# Revit family: Sink_Floor_8_Inch_Round-Zurn-FS8-5-Inch-Sump
name_source: partatom
category: Plumbing Fixtures
units: mm (PartAtom-declared; Revit-internal decimal feet)

## family parameters
Always vertical = Yes
Cut with Voids When Loaded = No
Maintain Annotation Orientation = No
OmniClass Number = 23.70.50.21.24.14
OmniClass Title = Deck Waste Water Drains
Part Type = Normal
Room Calculation Point = No
Round Connector Dimension = Use Radius
Shared = No
Work Plane-Based = No

## types (3) — shared parameters
Assembly Code = D2030300
Body Range = 5 "
CW Connection = No
Default Elevation = 20 "
Description = 8 [203] DIAMETER SANITARY PVC FLOOR SINK WITH 5 [127] SUMP DEPTH
Frame Height = 1.5 "
HW Connection = No
Main Material = Polyvinyl Chloride - Zurn - Polished
Manufacturer = Zurn Water, LLC
Manufacurer Brand = Zurn
Model = FS8
Modified Date = 12/12/2025
Overall Height = 7 "
Product Documentation Link = https://files.zurn.com
Product Installation Sheet = https://files.zurn.com
Product Page URL = https://www.zurn.com
Product data url = https://www.bimobject.com
Sanitary PVC floor sink = 10.625 "
URL = www.zurn.com
Vent Connection = No
WFU = 1
Waste Connection = Yes
Width = 8.625 "
zero-valued in all types: CWFU, HWFU

## per-type parameters (varying)
| type | Pipe Size A (Actual Radius) | Pipe Size A (Inner Radius) | Pipe Size A (Nominal Radius) |
| FS8-5-PV2-2 Inch Outlet | 1.188 " | 1.034 " | 1 " |
| FS8-5-PV3-3 Inch Outlet | 1.75 " | 1.534 " | 1.5 " |
| FS8-5-PV4-4 Inch Outlet | 2.25 " | 2.013 " | 2 " |

## geometry (parser evidence)
native form markers: Sweep x6
no freeform markers — native parametric forms only
